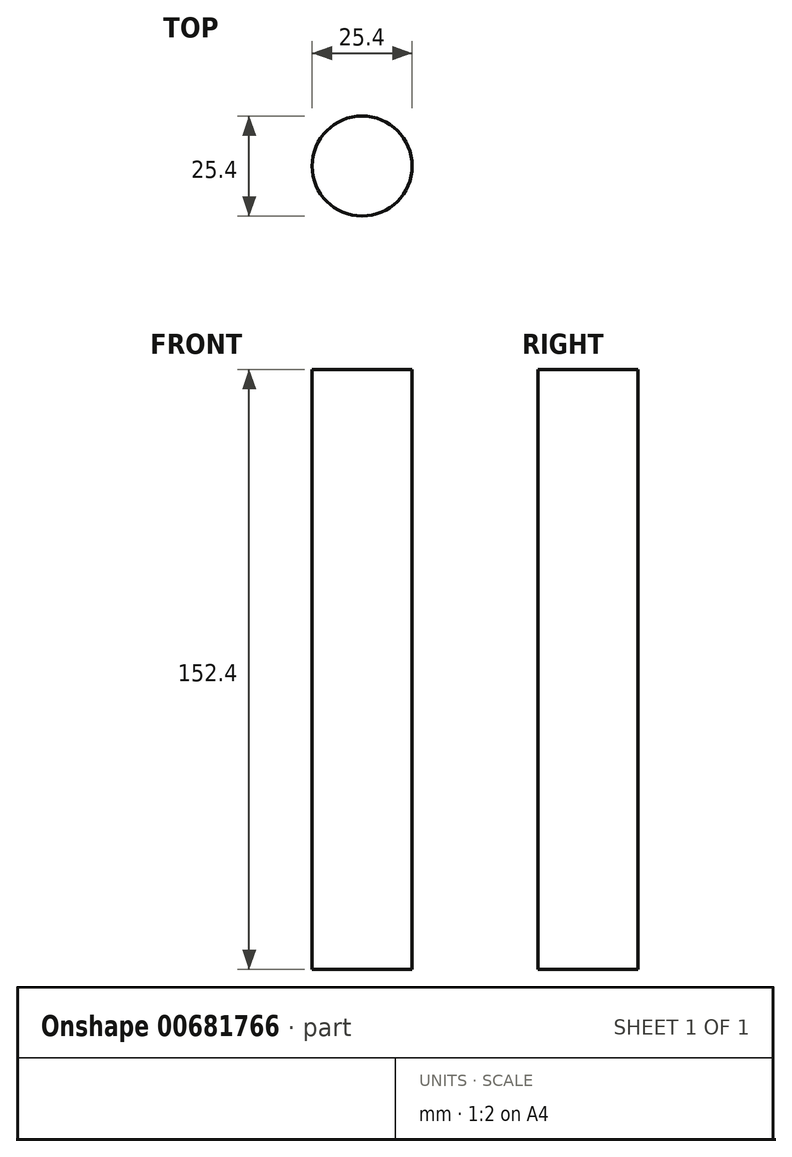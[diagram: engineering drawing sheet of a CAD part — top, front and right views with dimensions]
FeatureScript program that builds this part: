
annotation { "Feature Type Name" : "Feature", "Feature Type Description" : "" }
export const myFeature = defineFeature(function(context is Context, id is Id, definition is map)
    precondition{}
    {
        {
            var Q0;
            Q0=qCreatedBy(makeId("Top.planeOp"),FACE);
            var sketch = newSketch(context, id + "F0", { "sketchPlane" : qUnion([Q0])});
            skCircle(sketch, "E0", {"center": v(0, 0) * mm, "radius": 12.7 * mm});
            skSolve(sketch);
        }
        {
            var Q0;
            Q0=makeQuery(id+"F0.imprint","IMPRINT",FACE,{"disambiguationData":[TD([[makeQuery(id+"F0.imprint","IMPRINT",EDGE,{"derivedFrom":sQuery(id+"F0.wireOp",EDGE,"E0")}),1.0]])]});
            extrude(context, id + "F1", {"entities" : qUnion([Q0]), "depth" : 152.4 * mm, "offsetDistance" : 25.4 * mm});
        }
    });
